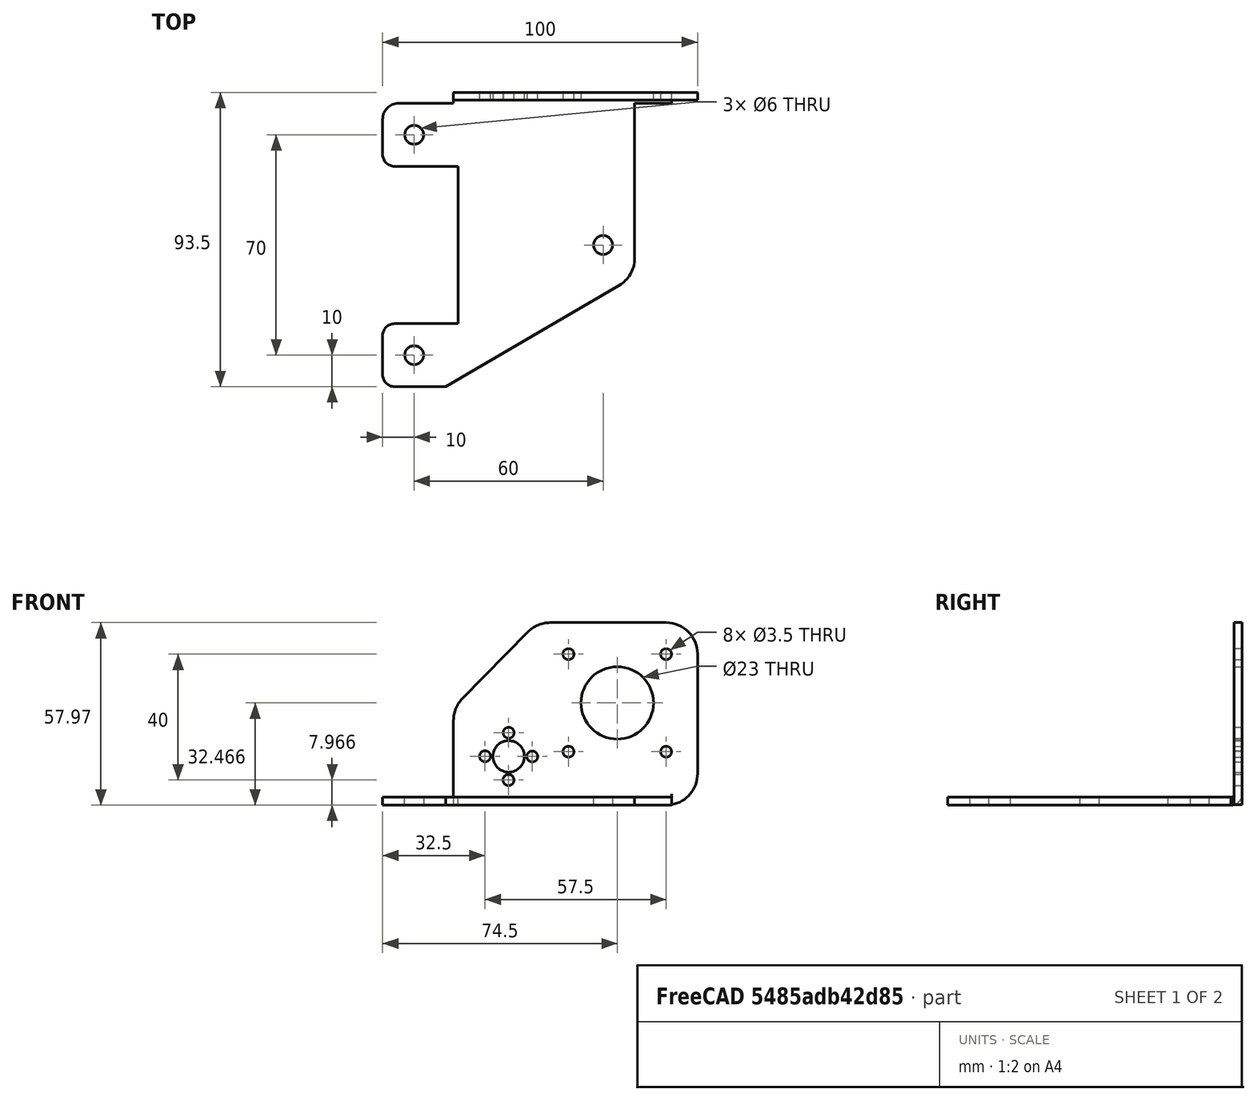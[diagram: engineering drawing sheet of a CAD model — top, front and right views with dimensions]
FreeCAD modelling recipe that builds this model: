
FCSTD DOCUMENT  (FreeCAD 0.19R24276 (Git))
Label: Z_extruder_plate_conv
License: All rights reserved
LicenseURL: http://en.wikipedia.org/wiki/All_rights_reserved
objects: Sketcher::SketchObject×2, PartDesign::Pad×1, PartDesign::FeaturePython×1, PartDesign::Body×1
note: 6 computed .brp shape members not serialized (recipe doc carries the construction recipe); baked Part::Feature solids carry a one-line shape summary decoded from their .brp

FEATURE [Sketcher::SketchObject] Sketch
  FullyConstrained = false
  sketch-geometry (37):
    g0: Circle CenterX=0 CenterY=0 CenterZ=0 NormalX=0 NormalY=0 NormalZ=-1 AngleXU=0 Radius=3
    g1: Circle CenterX=0 CenterY=70 CenterZ=0 NormalX=0 NormalY=0 NormalZ=-1 AngleXU=0 Radius=3
    g2: Circle CenterX=60 CenterY=35 CenterZ=0 NormalX=0 NormalY=0 NormalZ=-1 AngleXU=0 Radius=3
    g3: LineSegment StartX=10 StartY=-10 StartZ=0 EndX=-5.88033 EndY=-10 EndZ=0
    g4: LineSegment StartX=-5.88033 StartY=-10 StartZ=0 EndX=-6.2 EndY=-10 EndZ=0
    g5: ArcOfCircle CenterX=-6.2 CenterY=-6.2 CenterZ=0 NormalX=0 NormalY=0 NormalZ=1 AngleXU=-3.14159 Radius=3.8 StartAngle=0 EndAngle=1.5708
    g6: LineSegment StartX=-10 StartY=-6.2 StartZ=0 EndX=-10 EndY=6.2 EndZ=0
    g7: ArcOfCircle CenterX=-6.2 CenterY=6.2 CenterZ=0 NormalX=0 NormalY=0 NormalZ=1 AngleXU=-3.14159 Radius=3.8 StartAngle=4.71239 EndAngle=6.28319
    g8: LineSegment StartX=-6.2 StartY=10 StartZ=0 EndX=14 EndY=10 EndZ=0
    g9: LineSegment StartX=14 StartY=10 StartZ=0 EndX=14 EndY=60 EndZ=0
    g10: LineSegment StartX=14 StartY=60 StartZ=0 EndX=-6.2 EndY=60 EndZ=0
    g11: ArcOfCircle CenterX=-6.2 CenterY=63.8 CenterZ=0 NormalX=0 NormalY=0 NormalZ=1 AngleXU=-3.14159 Radius=3.8 StartAngle=0 EndAngle=1.5708
    g12: LineSegment StartX=-10 StartY=63.8 StartZ=0 EndX=-10 EndY=75 EndZ=0
    g13: ArcOfCircle CenterX=-5 CenterY=75 CenterZ=0 NormalX=0 NormalY=0 NormalZ=1 AngleXU=-3.14159 Radius=5 StartAngle=4.71239 EndAngle=6.28319
    g14: LineSegment StartX=-5 StartY=80 StartZ=0 EndX=12.5001 EndY=80 EndZ=0
    g15: LineSegment StartX=12.5001 StartY=80 StartZ=0 EndX=12.5001 EndY=106.913 EndZ=0
    g16: ArcOfCircle CenterX=22.5001 CenterY=106.913 CenterZ=0 NormalX=0 NormalY=0 NormalZ=1 AngleXU=-3.14159 Radius=10 StartAngle=5.50713 EndAngle=6.28319
    g17: LineSegment StartX=15.3632 StartY=113.917 StartZ=0 EndX=36.0601 EndY=135.005 EndZ=0
    g18: ArcOfCircle CenterX=43.197 CenterY=128 CenterZ=0 NormalX=0 NormalY=0 NormalZ=1 AngleXU=-3.14159 Radius=10 StartAngle=4.71239 EndAngle=5.50713
    g19: LineSegment StartX=43.197 StartY=138 StartZ=0 EndX=80 EndY=138 EndZ=0
    g20: ArcOfCircle CenterX=80 CenterY=128 CenterZ=0 NormalX=0 NormalY=0 NormalZ=1 AngleXU=-3.14159 Radius=10 StartAngle=3.14159 EndAngle=4.71239
    g21: LineSegment StartX=90 StartY=128 StartZ=0 EndX=90 EndY=90 EndZ=0
    g22: ArcOfCircle CenterX=80 CenterY=90 CenterZ=0 NormalX=0 NormalY=0 NormalZ=1 AngleXU=-3.14159 Radius=10 StartAngle=1.5708 EndAngle=3.14159
    g23: LineSegment StartX=80 StartY=80 StartZ=0 EndX=70 EndY=80 EndZ=0
    g24: LineSegment StartX=70 StartY=80 StartZ=0 EndX=70 EndY=30.7437 EndZ=0
    g25: ArcOfCircle CenterX=60 CenterY=30.7437 CenterZ=0 NormalX=0 NormalY=0 NormalZ=1 AngleXU=-3.14159 Radius=10 StartAngle=2.09887 EndAngle=3.14159
    g26: LineSegment StartX=65.0387 StartY=22.1059 StartZ=0 EndX=10 EndY=-10 EndZ=0
    g27: Circle CenterX=64.5 CenterY=112.5 CenterZ=0 NormalX=0 NormalY=0 NormalZ=-1 AngleXU=0 Radius=11.5
    g28: Circle CenterX=49 CenterY=128 CenterZ=0 NormalX=0 NormalY=0 NormalZ=-1 AngleXU=0 Radius=1.75
    g29: Circle CenterX=80 CenterY=128 CenterZ=0 NormalX=0 NormalY=0 NormalZ=-1 AngleXU=0 Radius=1.75
    g30: Circle CenterX=80 CenterY=97 CenterZ=0 NormalX=0 NormalY=0 NormalZ=-1 AngleXU=0 Radius=1.75
    g31: Circle CenterX=49 CenterY=97 CenterZ=0 NormalX=0 NormalY=0 NormalZ=-1 AngleXU=0 Radius=1.75
    g32: Circle CenterX=30 CenterY=95.5 CenterZ=0 NormalX=0 NormalY=0 NormalZ=-1 AngleXU=0 Radius=5
    g33: Circle CenterX=37.5 CenterY=95.4761 CenterZ=0 NormalX=0 NormalY=0 NormalZ=-1 AngleXU=0 Radius=1.75
    g34: Circle CenterX=22.5001 CenterY=95.5375 CenterZ=0 NormalX=0 NormalY=0 NormalZ=-1 AngleXU=0 Radius=1.75
    g35: Circle CenterX=30.0065 CenterY=103 CenterZ=0 NormalX=0 NormalY=0 NormalZ=-1 AngleXU=0 Radius=1.75
    g36: Circle CenterX=29.9584 CenterY=88.0001 CenterZ=0 NormalX=0 NormalY=0 NormalZ=-1 AngleXU=0 Radius=1.75
  constraints (7):
    c: Coincident(g7,g8)
    c: Coincident(g6,g7)
    c: Equal(g5,g7)
    c: Coincident(g5,g6)
    c: Coincident(g4,g5)
    c: Coincident(g3,g4)
    c: Coincident(g3,g26)
FEATURE [PartDesign::Pad] Pad
  Direction = (1,1,1)
  Length = 2.5
  Length2 = 100
  Profile = -> Sketch
  Type = 0
FEATURE [Sketcher::SketchObject] Sketch001
  ExternalGeometry = -> [Pad]
  FullyConstrained = false
  MapMode = 5
  Placement = pos=(0,0,2.5) rot=(0,0,1;0rad)
  Support = -> [Pad]
  sketch-geometry (1):
    g0: LineSegment StartX=81.7741 StartY=80 StartZ=0 EndX=-2.85894 EndY=80 EndZ=0
  constraints (2):
    c: Horizontal(g0)
    c: PointOnObject(g0,g-3)
FEATURE [PartDesign::FeaturePython] Fold  # WARN: FeaturePython — macro-defined, semantics opaque (R4)
  BaseFeature = -> Pad
  BendLine = -> Sketch001
  Position = 0
  angle = 90
  baseObject = -> Pad [Face39]
  invert = false
  invertbend = false
  kfactor = 0.5
  radius = 1
  unfold = false
FEATURE [PartDesign::Body] Body
  Group = -> [Sketch,Pad,Sketch001,Fold]
  Origin = -> Origin
  Tip = -> Fold
